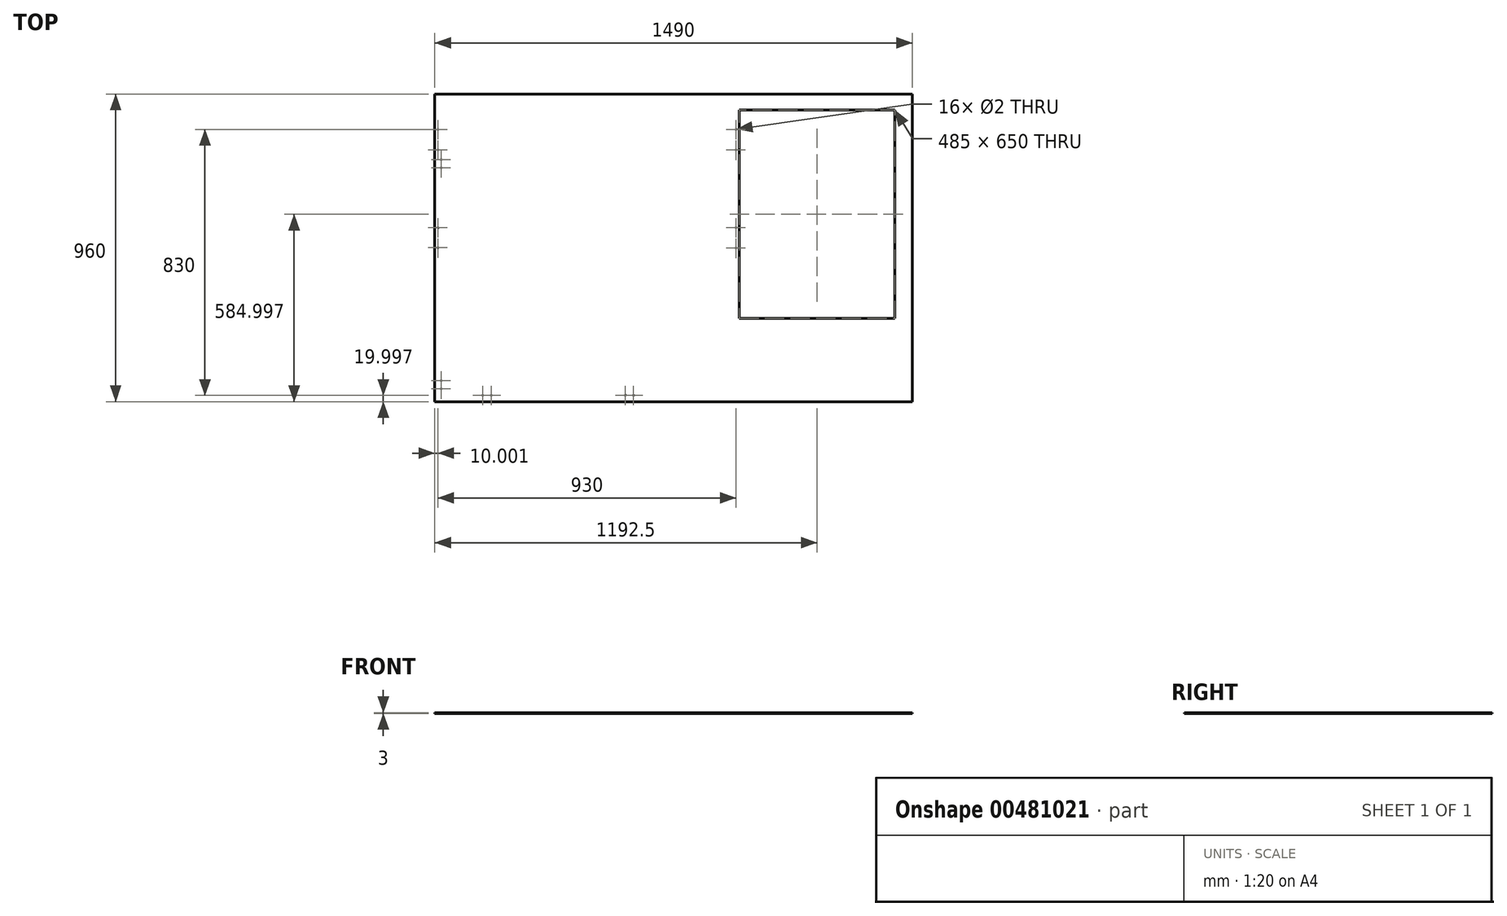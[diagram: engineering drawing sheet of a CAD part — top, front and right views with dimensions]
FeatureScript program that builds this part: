
annotation { "Feature Type Name" : "Feature", "Feature Type Description" : "" }
export const myFeature = defineFeature(function(context is Context, id is Id, definition is map)
    precondition{}
    {
        {
            var Q0;
            Q0=qCreatedBy(makeId("Top.planeOp"),FACE);
            var sketch = newSketch(context, id + "F0", { "sketchPlane" : qUnion([Q0])});
            skLineSegment(sketch, "E0.bottom", {"start": v(-731.48, 492.9) * mm, "end": v(758.52, 492.9) * mm});
            skLineSegment(sketch, "E0.top", {"start": v(-731.48, -467.1) * mm, "end": v(758.52, -467.1) * mm});
            skLineSegment(sketch, "E0.left", {"start": v(-731.48, 492.9) * mm, "end": v(-731.48, -467.1) * mm});
            skLineSegment(sketch, "E0.right", {"start": v(758.52, 492.9) * mm, "end": v(758.52, -467.1) * mm});
            skLineSegment(sketch, "E1.bottom", {"start": v(218.52, 442.9) * mm, "end": v(703.52, 442.9) * mm});
            skLineSegment(sketch, "E1.top", {"start": v(218.52, -207.1) * mm, "end": v(703.52, -207.1) * mm});
            skLineSegment(sketch, "E1.left", {"start": v(218.52, 442.9) * mm, "end": v(218.52, -207.1) * mm});
            skLineSegment(sketch, "E1.right", {"start": v(703.52, 442.9) * mm, "end": v(703.52, -207.1) * mm});
            skCircle(sketch, "E2", {"center": v(-581.48, -447.1) * mm, "radius": 1 * mm});
            skCircle(sketch, "E3", {"center": v(-555.48, -447.1) * mm, "radius": 1 * mm});
            skCircle(sketch, "E4", {"center": v(-111.48, -447.1) * mm, "radius": 1 * mm});
            skCircle(sketch, "E5", {"center": v(-137.48, -447.1) * mm, "radius": 1 * mm});
            skCircle(sketch, "E6", {"center": v(-711.48, 288.9) * mm, "radius": 1 * mm});
            skCircle(sketch, "E7", {"center": v(-711.48, 262.9) * mm, "radius": 1 * mm});
            skCircle(sketch, "E8", {"center": v(-711.48, -401.1) * mm, "radius": 1 * mm});
            skCircle(sketch, "E9", {"center": v(-711.48, -427.1) * mm, "radius": 1 * mm});
            skSolve(sketch);
        }
        {
            var Q0;
            Q0=makeQuery(id+"F0.imprint","IMPRINT",FACE,{"disambiguationData":[TD([[makeQuery(id+"F0.imprint","IMPRINT",EDGE,{"derivedFrom":sQuery(id+"F0.wireOp",EDGE,"E0.bottom")}),-1.0]])]});
            extrude(context, id + "F1", {"entities" : qUnion([Q0]), "offsetDistance" : 25 * mm, "depth" : 3 * mm});
        }
        {
            var Q0;
            Q0=makeQuery(id+"F1.opExtrude","CAP_FACE",FACE,{"disambiguationData":[OSD([sQuery(id+"F0.wireOp",EDGE,"E0.bottom"),sQuery(id+"F0.wireOp",EDGE,"E0.top"),sQuery(id+"F0.wireOp",EDGE,"E0.left"),sQuery(id+"F0.wireOp",EDGE,"E0.right"),sQuery(id+"F0.wireOp",EDGE,"E1.bottom"),sQuery(id+"F0.wireOp",EDGE,"E1.top"),sQuery(id+"F0.wireOp",EDGE,"E1.left"),sQuery(id+"F0.wireOp",EDGE,"E1.right")])],"isStart":false});
            var sketch = newSketch(context, id + "F2", { "sketchPlane" : qUnion([Q0])});
            skCircle(sketch, "E10", {"center": v(-721.48, 382.9) * mm, "radius": 1 * mm});
            skSolve(sketch);
        }
        {
            var Q0;
            Q0=makeQuery(id+"F2.imprint","IMPRINT",FACE,{"disambiguationData":[TD([[makeQuery(id+"F2.imprint","IMPRINT",EDGE,{"derivedFrom":sQuery(id+"F2.wireOp",EDGE,"E10")}),1.0]])]});
            extrude(context, id + "F3", {"entities" : qUnion([Q0]), "operationType" : NewBodyOperationType.REMOVE, "oppositeDirection" : true, "depth" : 3 * mm, "offsetDistance" : 25 * mm});
        }
        {
            var Q0;
            Q0=makeQuery(id+"F1.opExtrude","CAP_FACE",FACE,{"disambiguationData":[OSD([sQuery(id+"F0.wireOp",EDGE,"E0.bottom"),sQuery(id+"F0.wireOp",EDGE,"E0.top"),sQuery(id+"F0.wireOp",EDGE,"E0.left"),sQuery(id+"F0.wireOp",EDGE,"E0.right"),sQuery(id+"F0.wireOp",EDGE,"E1.bottom"),sQuery(id+"F0.wireOp",EDGE,"E1.top"),sQuery(id+"F0.wireOp",EDGE,"E1.left"),sQuery(id+"F0.wireOp",EDGE,"E1.right")])],"isStart":false});
            var sketch = newSketch(context, id + "F4", { "sketchPlane" : qUnion([Q0])});
            skCircle(sketch, "E11", {"center": v(208.52, 382.9) * mm, "radius": 1 * mm});
            skSolve(sketch);
        }
        {
            var Q0;
            Q0 = qSketchRegion(id + "F4", true);
            extrude(context, id + "F5", {"entities" : qUnion([Q0]), "operationType" : NewBodyOperationType.REMOVE, "oppositeDirection" : true, "depth" : 3 * mm, "offsetDistance" : 25 * mm});
        }
        {
            var Q0;
            Q0=makeQuery(id+"F1.opExtrude","CAP_FACE",FACE,{"disambiguationData":[OSD([sQuery(id+"F0.wireOp",EDGE,"E0.bottom"),sQuery(id+"F0.wireOp",EDGE,"E0.top"),sQuery(id+"F0.wireOp",EDGE,"E0.left"),sQuery(id+"F0.wireOp",EDGE,"E0.right"),sQuery(id+"F0.wireOp",EDGE,"E1.bottom"),sQuery(id+"F0.wireOp",EDGE,"E1.top"),sQuery(id+"F0.wireOp",EDGE,"E1.left"),sQuery(id+"F0.wireOp",EDGE,"E1.right")])],"isStart":false});
            var sketch = newSketch(context, id + "F6", { "sketchPlane" : qUnion([Q0])});
            skCircle(sketch, "E12", {"center": v(-721.48, 318.9) * mm, "radius": 1 * mm});
            skSolve(sketch);
        }
        {
            var Q0;
            Q0 = qSketchRegion(id + "F6", true);
            extrude(context, id + "F7", {"entities" : qUnion([Q0]), "operationType" : NewBodyOperationType.REMOVE, "oppositeDirection" : true, "depth" : 3 * mm, "offsetDistance" : 25 * mm});
        }
        {
            var Q0;
            Q0=makeQuery(id+"F1.opExtrude","CAP_FACE",FACE,{"disambiguationData":[OSD([sQuery(id+"F0.wireOp",EDGE,"E0.bottom"),sQuery(id+"F0.wireOp",EDGE,"E0.top"),sQuery(id+"F0.wireOp",EDGE,"E0.left"),sQuery(id+"F0.wireOp",EDGE,"E0.right"),sQuery(id+"F0.wireOp",EDGE,"E1.bottom"),sQuery(id+"F0.wireOp",EDGE,"E1.top"),sQuery(id+"F0.wireOp",EDGE,"E1.left"),sQuery(id+"F0.wireOp",EDGE,"E1.right")])],"isStart":false});
            var sketch = newSketch(context, id + "F8", { "sketchPlane" : qUnion([Q0])});
            skCircle(sketch, "E13", {"center": v(208.52, 318.4) * mm, "radius": 1 * mm});
            skSolve(sketch);
        }
        {
            var Q0;
            Q0 = qSketchRegion(id + "F8", true);
            extrude(context, id + "F9", {"entities" : qUnion([Q0]), "operationType" : NewBodyOperationType.REMOVE, "oppositeDirection" : true, "depth" : 3 * mm, "offsetDistance" : 25 * mm});
        }
        {
            var Q0;
            Q0=makeQuery(id+"F1.opExtrude","CAP_FACE",FACE,{"disambiguationData":[OSD([sQuery(id+"F0.wireOp",EDGE,"E0.bottom"),sQuery(id+"F0.wireOp",EDGE,"E0.top"),sQuery(id+"F0.wireOp",EDGE,"E0.left"),sQuery(id+"F0.wireOp",EDGE,"E0.right"),sQuery(id+"F0.wireOp",EDGE,"E1.bottom"),sQuery(id+"F0.wireOp",EDGE,"E1.top"),sQuery(id+"F0.wireOp",EDGE,"E1.left"),sQuery(id+"F0.wireOp",EDGE,"E1.right")])],"isStart":false});
            var sketch = newSketch(context, id + "F10", { "sketchPlane" : qUnion([Q0])});
            skCircle(sketch, "E14", {"center": v(-721.48, 76.4) * mm, "radius": 1 * mm});
            skSolve(sketch);
        }
        {
            var Q0;
            Q0=makeQuery(id+"F10.imprint","IMPRINT",FACE,{"disambiguationData":[TD([[makeQuery(id+"F10.imprint","IMPRINT",EDGE,{"derivedFrom":sQuery(id+"F10.wireOp",EDGE,"E14")}),-1.0]])]});
            var sketch = newSketch(context, id + "F11", { "sketchPlane" : qUnion([Q0])});
            skCircle(sketch, "E15", {"center": v(-721.48, 13.4) * mm, "radius": 1 * mm});
            skSolve(sketch);
        }
        {
            var Q0;
            Q0=makeQuery(id+"F10.imprint","IMPRINT",FACE,{"disambiguationData":[TD([[makeQuery(id+"F10.imprint","IMPRINT",EDGE,{"derivedFrom":sQuery(id+"F10.wireOp",EDGE,"E14")}),-1.0]])]});
            var sketch = newSketch(context, id + "F12", { "sketchPlane" : qUnion([Q0])});
            skCircle(sketch, "E16", {"center": v(208.52, 12.4) * mm, "radius": 1 * mm});
            skSolve(sketch);
        }
        {
            var Q0;
            Q0=makeQuery(id+"F10.imprint","IMPRINT",FACE,{"disambiguationData":[TD([[makeQuery(id+"F10.imprint","IMPRINT",EDGE,{"derivedFrom":sQuery(id+"F10.wireOp",EDGE,"E14")}),-1.0]])]});
            var sketch = newSketch(context, id + "F13", { "sketchPlane" : qUnion([Q0])});
            skCircle(sketch, "E17", {"center": v(208.52, 76.4) * mm, "radius": 1 * mm});
            skSolve(sketch);
        }
        {
            var Q0;
            Q0 = qSketchRegion(id + "F10", true);
            extrude(context, id + "F14", {"entities" : qUnion([Q0]), "operationType" : NewBodyOperationType.REMOVE, "oppositeDirection" : true, "depth" : 3 * mm, "offsetDistance" : 25 * mm});
        }
        {
            var Q0;
            Q0 = qSketchRegion(id + "F11", true);
            extrude(context, id + "F15", {"entities" : qUnion([Q0]), "operationType" : NewBodyOperationType.REMOVE, "oppositeDirection" : true, "depth" : 3 * mm, "offsetDistance" : 25 * mm});
        }
        {
            var Q0;
            Q0 = qSketchRegion(id + "F12", true);
            extrude(context, id + "F16", {"entities" : qUnion([Q0]), "operationType" : NewBodyOperationType.REMOVE, "oppositeDirection" : true, "depth" : 3 * mm, "offsetDistance" : 25 * mm});
        }
        {
            var Q0;
            Q0 = qSketchRegion(id + "F13", true);
            extrude(context, id + "F17", {"entities" : qUnion([Q0]), "operationType" : NewBodyOperationType.REMOVE, "oppositeDirection" : true, "depth" : 3 * mm, "offsetDistance" : 25 * mm});
        }
        {
            var Q0;
            Q0 = qSketchRegion(id + "F0", true);
            extrude(context, id + "F18", {"entities" : qUnion([Q0]), "operationType" : NewBodyOperationType.REMOVE, "flatOperationType" : FlatOperationType.REMOVE, "oppositeDirection" : true, "depth" : 25 * mm, "offsetDistance" : 25 * mm, "domain" : OperationDomain.MODEL});
        }
    });
